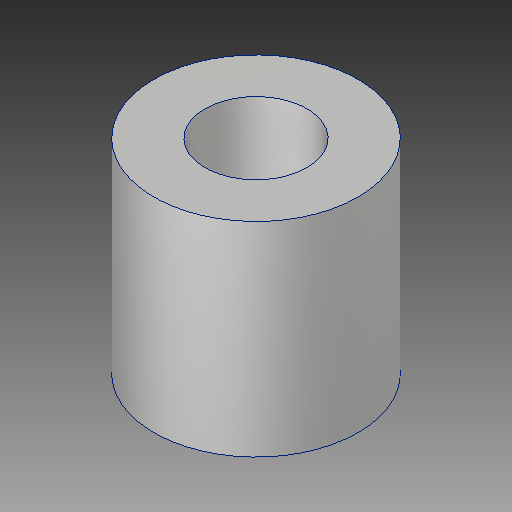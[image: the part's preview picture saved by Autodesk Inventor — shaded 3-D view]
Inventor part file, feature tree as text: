
AUTODESK INVENTOR PART (.ipt)
format: ipt  version: 2017 (Build 210142000, 142)  size: 105,984 bytes
history: native  units: in
note: dims shown in document units (in); Inventor stores cm internally (conversion verified against a paired STEP export)
features: extrude x1, sketch x1
ambient origin geometry x8: Origin, YZ Plane, XZ Plane, XY Plane, X Axis, Y Axis, Z Axis, Center Point
bodies: Solid1 (feature_tree)
feature tree (2):
  extrude  "Extrusion1"  Depth=0.5in
  sketch  "Sketch1"  dims[d0=0.25in d1=0.5in d2=0.5in d3=0.0in]
